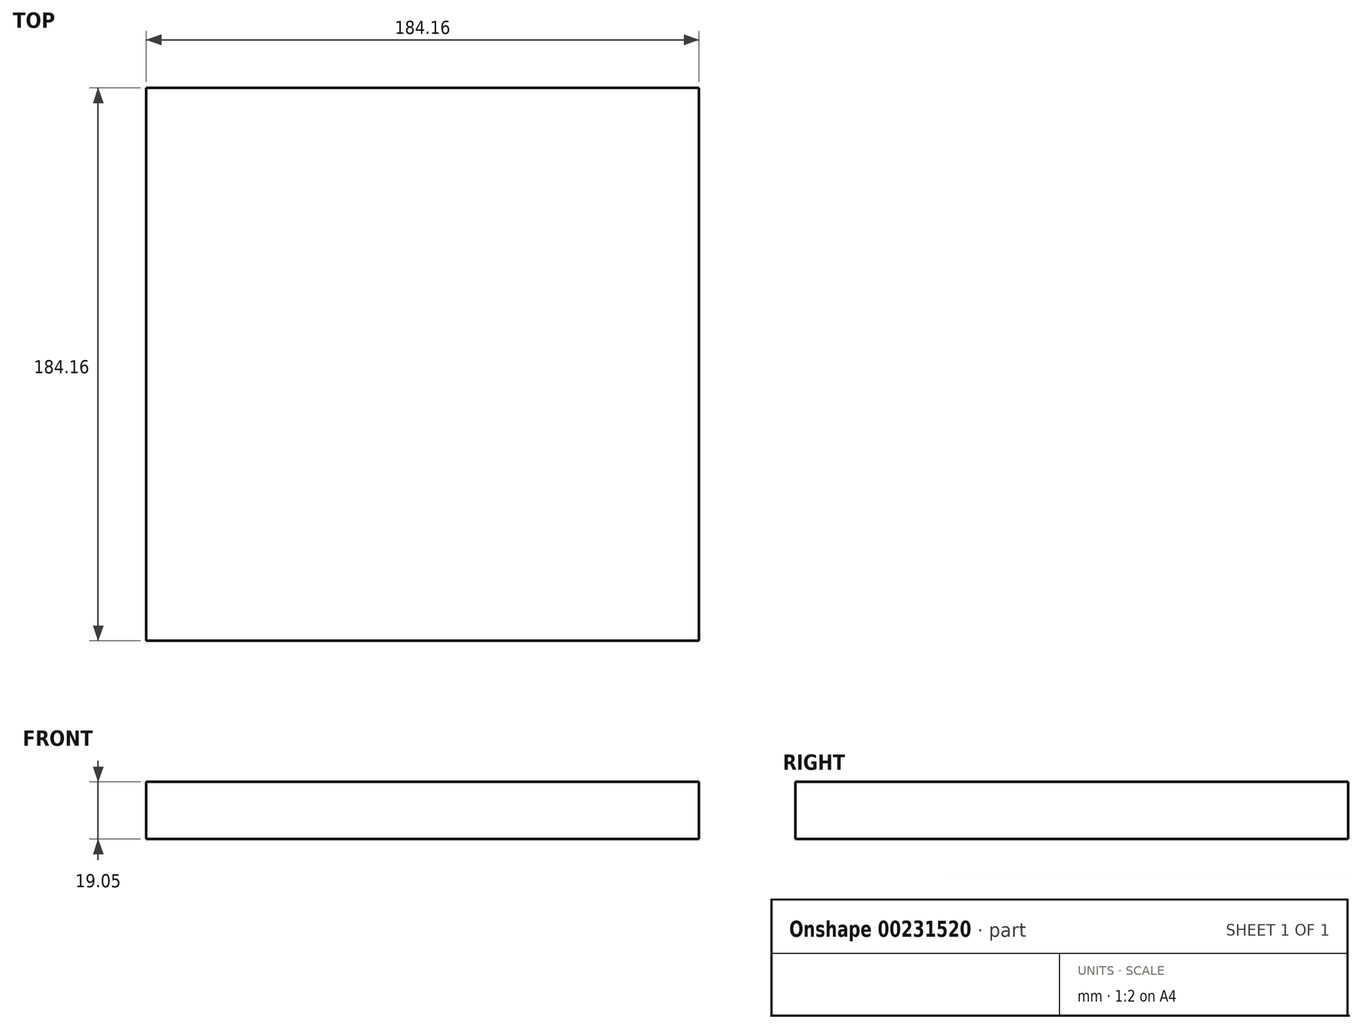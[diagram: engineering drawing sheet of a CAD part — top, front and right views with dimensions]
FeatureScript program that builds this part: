
annotation { "Feature Type Name" : "Feature", "Feature Type Description" : "" }
export const myFeature = defineFeature(function(context is Context, id is Id, definition is map)
    precondition{}
    {
        {
            var Q0;
            Q0=qCreatedBy(makeId("Top.planeOp"),FACE);
            var sketch = newSketch(context, id + "F0", { "sketchPlane" : qUnion([Q0])});
            skLineSegment(sketch, "E0.bottom", {"start": v(92.07, -92.07) * mm, "end": v(-92.08, -92.08) * mm});
            skLineSegment(sketch, "E0.top", {"start": v(92.07, 92.08) * mm, "end": v(-92.08, 92.08) * mm});
            skLineSegment(sketch, "E0.left", {"start": v(92.07, -92.07) * mm, "end": v(92.08, 92.08) * mm});
            skLineSegment(sketch, "E0.right", {"start": v(-92.08, -92.07) * mm, "end": v(-92.08, 92.07) * mm});
            skPoint(sketch, "E0.middle", {"position": v(0, 0) * mm});
            skSolve(sketch);
        }
        {
            var Q0;
            Q0=makeQuery(id+"F0.imprint","IMPRINT",FACE,{"disambiguationData":[TD([[makeQuery(id+"F0.imprint","IMPRINT",EDGE,{"derivedFrom":sQuery(id+"F0.wireOp",EDGE,"E0.bottom")}),-1.0]])]});
            extrude(context, id + "F1", {"entities" : qUnion([Q0]), "depth" : 19.05 * mm});
        }
    });
